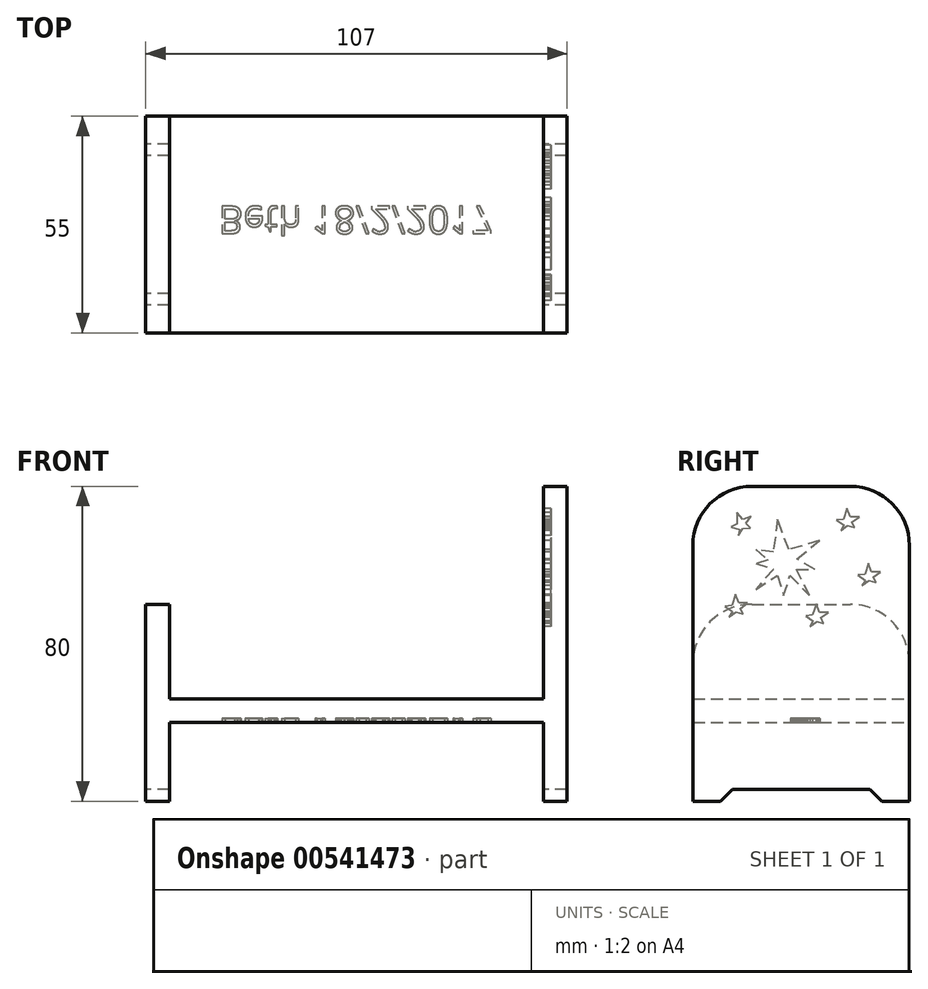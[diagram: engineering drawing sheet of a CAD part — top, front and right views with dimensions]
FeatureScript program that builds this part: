
annotation { "Feature Type Name" : "Feature", "Feature Type Description" : "" }
export const myFeature = defineFeature(function(context is Context, id is Id, definition is map)
    precondition{}
    {
        {
            var Q0;
            Q0=qCreatedBy(makeId("Front.planeOp"),FACE);
            var sketch = newSketch(context, id + "F0", { "sketchPlane" : qUnion([Q0])});
            skLineSegment(sketch, "E0", {"start": v(0, 0) * mm, "end": v(0, 50) * mm});
            skLineSegment(sketch, "E1", {"start": v(0, 50) * mm, "end": v(6, 50) * mm});
            skLineSegment(sketch, "E2", {"start": v(6, 50) * mm, "end": v(6, 26) * mm});
            skLineSegment(sketch, "E3", {"start": v(6, 26) * mm, "end": v(101, 26) * mm});
            skLineSegment(sketch, "E4", {"start": v(101, 26) * mm, "end": v(101, 80) * mm});
            skLineSegment(sketch, "E5", {"start": v(101, 80) * mm, "end": v(107, 80) * mm});
            skLineSegment(sketch, "E6", {"start": v(107, 80) * mm, "end": v(107, 0) * mm});
            skLineSegment(sketch, "E7", {"start": v(107, 0) * mm, "end": v(101, 0) * mm});
            skLineSegment(sketch, "E8", {"start": v(101, 0) * mm, "end": v(101, 20) * mm});
            skLineSegment(sketch, "E9", {"start": v(101, 20) * mm, "end": v(6, 20) * mm});
            skLineSegment(sketch, "E10", {"start": v(6, 20) * mm, "end": v(6, 0) * mm});
            skLineSegment(sketch, "E11", {"start": v(6, 0) * mm, "end": v(0, 0) * mm});
            skSolve(sketch);
        }
        {
            var Q0;
            Q0=makeQuery(id+"F0.imprint","IMPRINT",FACE,{"disambiguationData":[TD([[makeQuery(id+"F0.imprint","IMPRINT",EDGE,{"derivedFrom":sQuery(id+"F0.wireOp",EDGE,"E0")}),-1.0]])]});
            extrude(context, id + "F1", {"entities" : qUnion([Q0]), "depth" : 55 * mm, "offsetDistance" : 25 * mm});
        }
        {
            var Q0;
            Q0=makeQuery(id+"F1.opExtrude","CAP_EDGE",EDGE,{"disambiguationData":[OSD([sQuery(id+"F0.wireOp",EDGE,"E5")])],"isStart":false});
            var Q1;
            Q1=makeQuery(id+"F1.opExtrude","CAP_EDGE",EDGE,{"disambiguationData":[OSD([sQuery(id+"F0.wireOp",EDGE,"E5")])],"isStart":true});
            var Q2;
            Q2=makeQuery(id+"F1.opExtrude","CAP_EDGE",EDGE,{"disambiguationData":[OSD([sQuery(id+"F0.wireOp",EDGE,"E1")])],"isStart":false});
            var Q3;
            Q3=makeQuery(id+"F1.opExtrude","CAP_EDGE",EDGE,{"disambiguationData":[OSD([sQuery(id+"F0.wireOp",EDGE,"E1")])],"isStart":true});
            fillet(context, id + "F2", {"entities" : qUnion([Q0, Q1, Q2, Q3]), "radius" : 15 * mm, "tangentPropagation" : true, "allowEdgeOverflow" : false});
        }
        {
            var Q0;
            Q0=makeQuery(id+"F1.opExtrude","SWEPT_FACE",FACE,{"disambiguationData":[OSD([sQuery(id+"F0.wireOp",EDGE,"E0")])]});
            var sketch = newSketch(context, id + "F3", { "sketchPlane" : qUnion([Q0])});
            skLineSegment(sketch, "E12", {"start": v(7, 0) * mm, "end": v(10, 3) * mm});
            skLineSegment(sketch, "E13", {"start": v(10, 3) * mm, "end": v(45, 3) * mm});
            skLineSegment(sketch, "E14", {"start": v(45, 3) * mm, "end": v(48, 0) * mm});
            skLineSegment(sketch, "E15", {"start": v(48, 0) * mm, "end": v(7, 0) * mm});
            skSolve(sketch);
        }
        {
            var Q0;
            Q0=makeQuery(id+"F3.imprint","IMPRINT",FACE,{"disambiguationData":[TD([[makeQuery(id+"F3.imprint","IMPRINT",EDGE,{"derivedFrom":sQuery(id+"F3.wireOp",EDGE,"E12")}),-1.0]])]});
            extrude(context, id + "F4", {"entities" : qUnion([Q0]), "operationType" : NewBodyOperationType.REMOVE, "endBound" : BoundingType.THROUGH_ALL, "oppositeDirection" : true, "depth" : 25 * mm, "offsetDistance" : 25 * mm});
        }
        {
            var Q0;
            Q0=makeQuery(id+"F1.opExtrude","SWEPT_FACE",FACE,{"disambiguationData":[OSD([sQuery(id+"F0.wireOp",EDGE,"E4")])]});
            var sketch = newSketch(context, id + "F5", { "sketchPlane" : qUnion([Q0])});
            skLineSegment(sketch, "E16", {"start": v(33.33, 71.07) * mm, "end": v(33.5, 71.63) * mm});
            skLineSegment(sketch, "E17", {"start": v(33.5, 71.63) * mm, "end": v(34.58, 63.32) * mm});
            skLineSegment(sketch, "E18", {"start": v(34.58, 63.32) * mm, "end": v(39.03, 63.9) * mm});
            skLineSegment(sketch, "E19", {"start": v(39.03, 63.9) * mm, "end": v(35.9, 61.3) * mm});
            skLineSegment(sketch, "E20", {"start": v(35.9, 61.3) * mm, "end": v(39.03, 60.36) * mm});
            skLineSegment(sketch, "E21", {"start": v(39.03, 60.36) * mm, "end": v(34.58, 58.94) * mm});
            skLineSegment(sketch, "E22", {"start": v(34.58, 58.94) * mm, "end": v(39.03, 53.78) * mm});
            skLineSegment(sketch, "E23", {"start": v(39.03, 53.78) * mm, "end": v(33.5, 57.39) * mm});
            skLineSegment(sketch, "E24", {"start": v(33.5, 57.39) * mm, "end": v(31.95, 52.2) * mm});
            skLineSegment(sketch, "E25", {"start": v(31.95, 52.2) * mm, "end": v(30.3, 57.39) * mm});
            skLineSegment(sketch, "E26", {"start": v(30.3, 57.39) * mm, "end": v(25.42, 52.2) * mm});
            skLineSegment(sketch, "E27", {"start": v(25.42, 52.2) * mm, "end": v(28.65, 58.94) * mm});
            skLineSegment(sketch, "E28", {"start": v(28.65, 58.94) * mm, "end": v(24, 58.94) * mm});
            skLineSegment(sketch, "E29", {"start": v(24, 58.94) * mm, "end": v(28.52, 61.51) * mm});
            skLineSegment(sketch, "E30", {"start": v(28.52, 61.51) * mm, "end": v(22.9, 66.2) * mm});
            skLineSegment(sketch, "E31", {"start": v(22.9, 66.2) * mm, "end": v(30.62, 63.9) * mm});
            skLineSegment(sketch, "E32", {"start": v(30.62, 63.9) * mm, "end": v(33.33, 71.07) * mm});
            skLineSegment(sketch, "E33", {"start": v(15, 72.24) * mm, "end": v(15.83, 74.41) * mm});
            skLineSegment(sketch, "E34", {"start": v(15.83, 74.41) * mm, "end": v(16.74, 71.63) * mm});
            skLineSegment(sketch, "E35", {"start": v(16.74, 71.63) * mm, "end": v(18.5, 71.4) * mm});
            skLineSegment(sketch, "E36", {"start": v(18.5, 71.4) * mm, "end": v(16.61, 70.12) * mm});
            skLineSegment(sketch, "E37", {"start": v(16.61, 70.12) * mm, "end": v(17.44, 68.74) * mm});
            skLineSegment(sketch, "E38", {"start": v(17.44, 68.74) * mm, "end": v(15.7, 70.03) * mm});
            skLineSegment(sketch, "E39", {"start": v(15.7, 70.03) * mm, "end": v(13.95, 69.5) * mm});
            skLineSegment(sketch, "E40", {"start": v(13.95, 69.5) * mm, "end": v(14.59, 70.95) * mm});
            skLineSegment(sketch, "E41", {"start": v(14.59, 70.95) * mm, "end": v(12.74, 72.24) * mm});
            skLineSegment(sketch, "E42", {"start": v(12.74, 72.24) * mm, "end": v(15, 72.24) * mm});
            skLineSegment(sketch, "E43", {"start": v(42.34, 71.58) * mm, "end": v(43.86, 73.35) * mm});
            skLineSegment(sketch, "E44", {"start": v(43.86, 73.35) * mm, "end": v(43.77, 70.42) * mm});
            skLineSegment(sketch, "E45", {"start": v(43.77, 70.42) * mm, "end": v(45.35, 69.6) * mm});
            skLineSegment(sketch, "E46", {"start": v(45.35, 69.6) * mm, "end": v(43.13, 69.04) * mm});
            skLineSegment(sketch, "E47", {"start": v(43.13, 69.04) * mm, "end": v(43.44, 67.46) * mm});
            skLineSegment(sketch, "E48", {"start": v(43.44, 67.46) * mm, "end": v(42.23, 69.27) * mm});
            skLineSegment(sketch, "E49", {"start": v(42.23, 69.27) * mm, "end": v(40.42, 69.37) * mm});
            skLineSegment(sketch, "E50", {"start": v(40.42, 69.37) * mm, "end": v(41.51, 70.51) * mm});
            skLineSegment(sketch, "E51", {"start": v(41.51, 70.51) * mm, "end": v(40.21, 72.36) * mm});
            skLineSegment(sketch, "E52", {"start": v(40.21, 72.36) * mm, "end": v(42.34, 71.58) * mm});
            skLineSegment(sketch, "E53", {"start": v(43.35, 50.3) * mm, "end": v(44.18, 52.48) * mm});
            skLineSegment(sketch, "E54", {"start": v(44.18, 52.48) * mm, "end": v(45.1, 49.7) * mm});
            skLineSegment(sketch, "E55", {"start": v(45.1, 49.7) * mm, "end": v(46.85, 49.47) * mm});
            skLineSegment(sketch, "E56", {"start": v(46.85, 49.47) * mm, "end": v(44.96, 48.18) * mm});
            skLineSegment(sketch, "E57", {"start": v(44.96, 48.18) * mm, "end": v(45.8, 46.8) * mm});
            skLineSegment(sketch, "E58", {"start": v(45.8, 46.8) * mm, "end": v(44.04, 48.1) * mm});
            skLineSegment(sketch, "E59", {"start": v(44.04, 48.1) * mm, "end": v(42.3, 47.56) * mm});
            skLineSegment(sketch, "E60", {"start": v(42.3, 47.56) * mm, "end": v(42.94, 49.01) * mm});
            skLineSegment(sketch, "E61", {"start": v(42.94, 49.01) * mm, "end": v(41.09, 50.3) * mm});
            skLineSegment(sketch, "E62", {"start": v(41.09, 50.3) * mm, "end": v(43.35, 50.3) * mm});
            skLineSegment(sketch, "E63", {"start": v(22.84, 47.91) * mm, "end": v(23.67, 50.09) * mm});
            skLineSegment(sketch, "E64", {"start": v(23.67, 50.09) * mm, "end": v(24.58, 47.3) * mm});
            skLineSegment(sketch, "E65", {"start": v(24.58, 47.3) * mm, "end": v(26.34, 47.08) * mm});
            skLineSegment(sketch, "E66", {"start": v(26.34, 47.08) * mm, "end": v(24.45, 45.8) * mm});
            skLineSegment(sketch, "E67", {"start": v(24.45, 45.8) * mm, "end": v(25.28, 44.41) * mm});
            skLineSegment(sketch, "E68", {"start": v(25.28, 44.41) * mm, "end": v(23.53, 45.7) * mm});
            skLineSegment(sketch, "E69", {"start": v(23.53, 45.7) * mm, "end": v(21.8, 45.17) * mm});
            skLineSegment(sketch, "E70", {"start": v(21.8, 45.17) * mm, "end": v(22.43, 46.62) * mm});
            skLineSegment(sketch, "E71", {"start": v(22.43, 46.62) * mm, "end": v(20.58, 47.91) * mm});
            skLineSegment(sketch, "E72", {"start": v(20.58, 47.91) * mm, "end": v(22.84, 47.91) * mm});
            skLineSegment(sketch, "E73", {"start": v(9.6, 58.26) * mm, "end": v(10.42, 60.43) * mm});
            skLineSegment(sketch, "E74", {"start": v(10.42, 60.43) * mm, "end": v(11.33, 57.65) * mm});
            skLineSegment(sketch, "E75", {"start": v(11.33, 57.65) * mm, "end": v(13.09, 57.43) * mm});
            skLineSegment(sketch, "E76", {"start": v(13.09, 57.43) * mm, "end": v(11.2, 56.14) * mm});
            skLineSegment(sketch, "E77", {"start": v(11.2, 56.14) * mm, "end": v(12.03, 54.76) * mm});
            skLineSegment(sketch, "E78", {"start": v(12.03, 54.76) * mm, "end": v(10.28, 56.05) * mm});
            skLineSegment(sketch, "E79", {"start": v(10.28, 56.05) * mm, "end": v(8.54, 55.52) * mm});
            skLineSegment(sketch, "E80", {"start": v(8.54, 55.52) * mm, "end": v(9.18, 56.97) * mm});
            skLineSegment(sketch, "E81", {"start": v(9.18, 56.97) * mm, "end": v(7.33, 58.26) * mm});
            skLineSegment(sketch, "E82", {"start": v(7.33, 58.26) * mm, "end": v(9.6, 58.26) * mm});
            skSolve(sketch);
        }
        {
            var Q0;
            Q0 = qSketchRegion(id + "F5", true);
            extrude(context, id + "F6", {"entities" : qUnion([Q0]), "operationType" : NewBodyOperationType.REMOVE, "oppositeDirection" : true, "depth" : 2 * mm, "offsetDistance" : 25 * mm});
        }
        {
            var Q0;
            Q0=makeQuery(id+"F1.opExtrude","SWEPT_FACE",FACE,{"disambiguationData":[OSD([sQuery(id+"F0.wireOp",EDGE,"E9")])]});
            var sketch = newSketch(context, id + "F7", { "sketchPlane" : qUnion([Q0])});
            skText(sketch, "E83", { "text": "Beth 18/2/2017", "fontName": "OpenSans-Regular.ttf"});
            const initialGuessF7  = {"E83": [0.01843, 0.02285, 1, 0, 0.00701]};
            skSetInitialGuess(sketch, initialGuessF7);
            skSolve(sketch);
        }
        {
            var Q0;
            Q0 = qSketchRegion(id + "F7", true);
            extrude(context, id + "F8", {"entities" : qUnion([Q0]), "operationType" : NewBodyOperationType.REMOVE, "oppositeDirection" : true, "depth" : 1 * mm, "offsetDistance" : 25 * mm});
        }
    });
